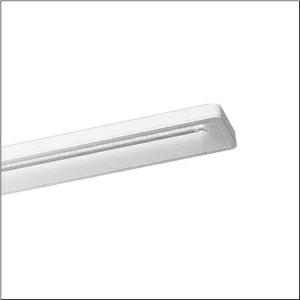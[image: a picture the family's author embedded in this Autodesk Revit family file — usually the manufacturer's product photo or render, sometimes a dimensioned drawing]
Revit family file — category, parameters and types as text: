
# Revit family: taris_r__21_5mt216704wd_b9ab
name_source: partatom
category: Lighting Fixtures
units: mm (PartAtom-declared; Revit-internal decimal feet)

## family parameters
Cut with Voids When Loaded = No
Host = Face
Light Source = No
Part Type = Normal
Room Calculation Point = No
Round Connector Dimension = Use Diameter
Shared = No

## types (1)
- Taris® 21 (1 x LED, 4910 lm, 30.6 W, 4000K)
    Apparent Load = 31 VA
    CIE Flux Codes = 73 96 99 100 100
    Color Rendering = 80
    Color Temperature = 4000K
    Default Elevation = 1800 mm
    Description = Taris® 21, office luminaire, primary anti-glare with micro louvre, primary optical cover: axial lens, of PMMA, structured, CAT 2 (L<= 1500cd/m²), light emission: direct distribution, primary light characteristic: symmetric, installation type: surface-mounted, LED, rated luminous flux: 4.910lm, luminous efficacy: 160lm/W, light colour: 840, colour temperature: 4000K, control gear: ECG, with terminal, 5-pole, mains connection: 230V, AC, 50Hz, rated input power: 31W, housing, luminaire housing, of plastic, traffic white (RAL 9016), length: 1.230mm, width: 134mm, height: 50mm, protection rating (complete): IP20, insulation class (complete): insulation class I (protective earthing), certification: CE, ENEC, VDE, protection symbol: F, impact resistance: IK02, permissible operating ambient temperature: 0..+35°C, standard: EN 50419, packaging unit: 1 piece
    Height = 51 mm
    Lamp = 1 x LED
    Lamp Light Flux = 4910 lm
    Lamp Power = 30.6 W
    Lamp count = 1
    Length = 1233 mm
    Luminous efficacy = 160 lm/W
    Manufacturer = Siteco
    ModVariant = No
    Model = 5MT216704WD
    Mounting Place = Ceiling
    Mounting Type = Surface mounted
    Number of Poles = 1
    OnlyDefault = Yes
    Power Factor = 1
    Product Name = Taris® 21
    Product group = office luminaire | ceiling mounted
    ProductGroupID = 304
    Protection Class = Protection class I
    Protection Degree = IP 20
    RLX_Detail_Level = 1
    RLX_Emergency_Light_Flux = 0 lm
    RLX_Emergency_Type = 0
    RLX_Emergency_Type_DB = No
    RlxData = <blob elided: 39057 chars, md5=1e408a43>
    Socket = socket
    Standby Power = 0 W
    System Light Flux = 4910 lm
    System Power = 31 W
    Type Comments = Product without accessories
    Type Image = l_1004728.jpg
    URL = http://relux.com
    VarID = ---
    Voltage = 0 V
    Weight = 0.00 kg
    Width = 134 mm

## geometry (parser evidence)
native form markers: Blend x4, Sweep x8
no freeform markers — native parametric forms only
